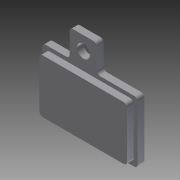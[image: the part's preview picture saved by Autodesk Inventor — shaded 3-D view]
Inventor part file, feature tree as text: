
AUTODESK INVENTOR PART (.ipt)
format: ipt  version: 2011 (Build 150239000, 239)  size: 125,440 bytes
history: native  units: in
note: dims shown in document units (in); Inventor stores cm internally (conversion verified against a paired STEP export)
features: sketch x4, extrude x3, hole x1, fillet x1
ambient origin geometry x8: Origin, YZ Plane, XZ Plane, XY Plane, X Axis, Y Axis, Z Axis, Center Point
bodies: Solid1 (feature_tree)
feature tree (9):
  extrude  "Extrusion1"  Depth=0.3543in
  extrude  "Extrusion2"  Depth=0.0222in
  extrude  "Extrusion3"  Depth=0.1575in
  hole  "Hole1"  [1 undecoded]
  fillet  "Fillet1"  Radius=0.0197in
  sketch  "Sketch1"  dims[d0=0.5512in d1=0.3543in]
  sketch  "Sketch2"  dims[d2=0.0787in d3=0.0in d4=0.0222in]
  sketch  "Sketch3"  dims[d5=0.0394in d6=0.0in d7=0.1575in]
  sketch  "Sketch4"  dims[d8=0.1575in d9=0.1575in d10=0.0in d11=0.075in d12=0.75in d13=0.375in d14=0.25in d15=0.5635in d16=1.0in d17=0.8108in d18=0.0197in]
note: 1 required parameter value undecoded (feature->parameter linkage not recoverable at this tier; creation-order binding heuristic only, values carry confidence <= 0.55)
